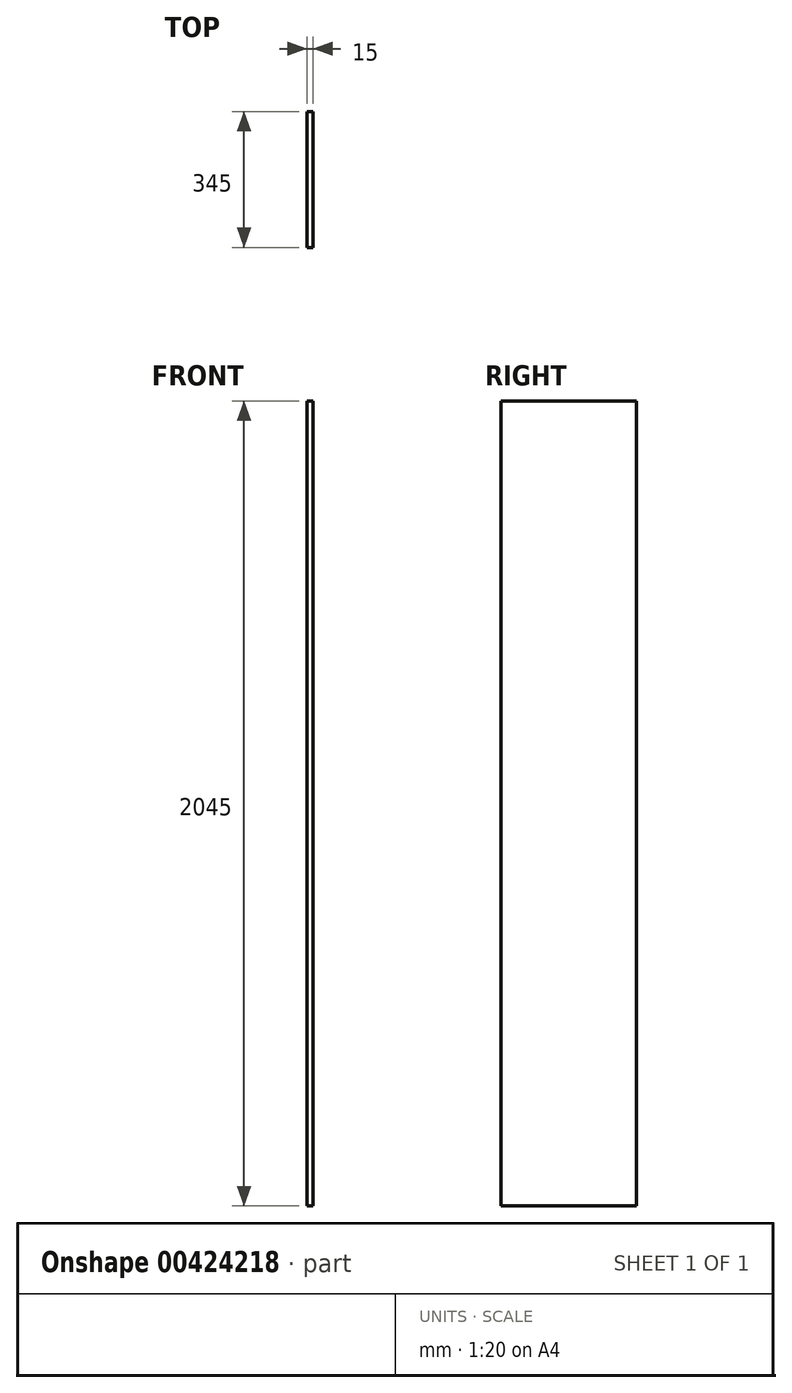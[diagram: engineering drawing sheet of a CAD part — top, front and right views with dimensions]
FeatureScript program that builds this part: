
annotation { "Feature Type Name" : "Feature", "Feature Type Description" : "" }
export const myFeature = defineFeature(function(context is Context, id is Id, definition is map)
    precondition{}
    {
        {
            var Q0;
            Q0=qCreatedBy(makeId("Right.planeOp"),FACE);
            var sketch = newSketch(context, id + "F0", { "sketchPlane" : qUnion([Q0])});
            skLineSegment(sketch, "E0.bottom", {"start": v(-783.1, 971.77) * mm, "end": v(-438.1, 971.77) * mm});
            skLineSegment(sketch, "E0.top", {"start": v(-783.1, -1073.23) * mm, "end": v(-438.1, -1073.23) * mm});
            skLineSegment(sketch, "E0.left", {"start": v(-783.1, 971.77) * mm, "end": v(-783.1, -1073.23) * mm});
            skLineSegment(sketch, "E0.right", {"start": v(-438.1, 971.77) * mm, "end": v(-438.1, -1073.23) * mm});
            skSolve(sketch);
        }
        {
            var Q0;
            Q0=makeQuery(id+"F0.imprint","IMPRINT",FACE,{"disambiguationData":[TD([[makeQuery(id+"F0.imprint","IMPRINT",EDGE,{"derivedFrom":sQuery(id+"F0.wireOp",EDGE,"E0.bottom")}),-1.0]])]});
            extrude(context, id + "F1", {"entities" : qUnion([Q0]), "depth" : 15 * mm});
        }
    });
